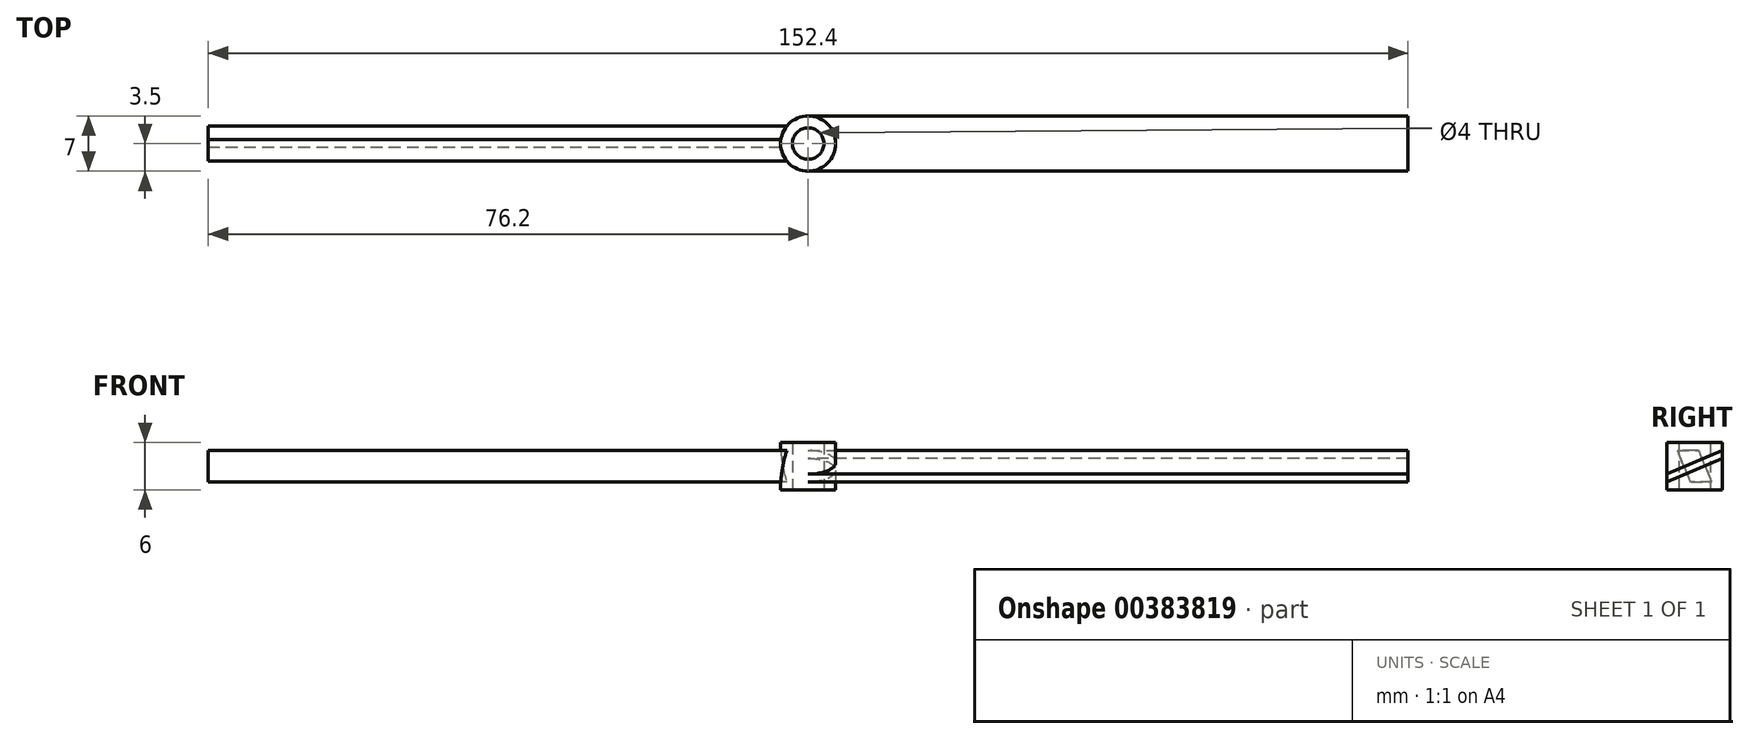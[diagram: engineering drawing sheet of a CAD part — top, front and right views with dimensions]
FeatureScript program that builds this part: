
annotation { "Feature Type Name" : "Feature", "Feature Type Description" : "" }
export const myFeature = defineFeature(function(context is Context, id is Id, definition is map)
    precondition{}
    {
        {
            var Q0;
            Q0=qCreatedBy(makeId("Top.planeOp"),FACE);
            var sketch = newSketch(context, id + "F0", { "sketchPlane" : qUnion([Q0])});
            skCircle(sketch, "E0", {"center": v(0, 0) * mm, "radius": 2 * mm});
            skLineSegment(sketch, "E1", {"start": v(0, 0) * mm, "end": v(2, 0) * mm});
            skLineSegment(sketch, "E2", {"start": v(0, 0) * mm, "end": v(76.2, 0) * mm});
            skLineSegment(sketch, "E3", {"start": v(0, 0) * mm, "end": v(-76.2, 0) * mm});
            skCircle(sketch, "E4", {"center": v(0, 0) * mm, "radius": 3.5 * mm});
            skLineSegment(sketch, "E5", {"start": v(0, 0) * mm, "end": v(0, 3.5) * mm});
            skLineSegment(sketch, "E6", {"start": v(0, 3.5) * mm, "end": v(0, -3.5) * mm});
            skLineSegment(sketch, "E7", {"start": v(0, 3.5) * mm, "end": v(-76.2, 3.5) * mm});
            skLineSegment(sketch, "E8", {"start": v(0, -3.5) * mm, "end": v(-76.2, -3.5) * mm});
            skLineSegment(sketch, "E9", {"start": v(-76.2, -3.5) * mm, "end": v(-76.2, 3.5) * mm});
            skLineSegment(sketch, "E10", {"start": v(0, 3.5) * mm, "end": v(76.2, 3.5) * mm});
            skLineSegment(sketch, "E11", {"start": v(0, -3.5) * mm, "end": v(76.2, -3.5) * mm});
            skLineSegment(sketch, "E12", {"start": v(76.2, -3.5) * mm, "end": v(76.2, 3.5) * mm});
            skSolve(sketch);
        }
        {
            var Q0;
            Q0=qSketchRegion(id+"F0",true);
            extrude(context, id + "F1", {"entities" : qUnion([Q0]), "depth" : 4 * mm});
        }
        {
            var Q0;
            Q0=makeQuery(id+"F1.opExtrude","CAP_FACE",FACE,{"disambiguationData":[OSD([sQuery(id+"F0.wireOp",EDGE,"E0"),sQuery(id+"F0.wireOp",EDGE,"E7"),sQuery(id+"F0.wireOp",EDGE,"E8"),sQuery(id+"F0.wireOp",EDGE,"E9"),sQuery(id+"F0.wireOp",EDGE,"E10"),sQuery(id+"F0.wireOp",EDGE,"E11"),sQuery(id+"F0.wireOp",EDGE,"E12")])],"isStart":false});
            var sketch = newSketch(context, id + "F2", { "sketchPlane" : qUnion([Q0])});
            skCircle(sketch, "E13", {"center": v(0, 0) * mm, "radius": 3.5 * mm});
            skLineSegment(sketch, "E14", {"start": v(0, 0) * mm, "end": v(3.5, 0) * mm});
            skLineSegment(sketch, "E15", {"start": v(3.5, 0) * mm, "end": v(-3.5, 0) * mm});
            skLineSegment(sketch, "E16", {"start": v(-3.5, 0) * mm, "end": v(-3.5, 3.5) * mm});
            skLineSegment(sketch, "E17", {"start": v(-3.5, 3.5) * mm, "end": v(-3.5, -3.5) * mm});
            skLineSegment(sketch, "E18", {"start": v(3.5, 0) * mm, "end": v(3.5, 3.5) * mm});
            skLineSegment(sketch, "E19", {"start": v(3.5, 3.5) * mm, "end": v(3.5, -3.5) * mm});
            skSolve(sketch);
        }
        {
            var Q0;
            {var subQ0=sQuery(id+"F2.wireOp",EDGE,"E17");var subQ1=sQuery(id+"F2.wireOp",EDGE,"E13");var subQ2=makeQuery(id+"F2.imprint","INTERSECT",VERTEX,{"derivedFrom":[subQ1,sQuery(id+"F2.wireOp",EDGE,"E15"),subQ0]});Q0=makeQuery(id+"F2.imprint","IMPRINT",FACE,{"disambiguationData":[TD([[makeQuery(id+"F2.imprint","IMPRINT",EDGE,{"disambiguationData":[TD([[subQ2,1.0]])],"derivedFrom":subQ1}),-1.0]])]});}
            var Q1;
            {var subQ0=sQuery(id+"F2.wireOp",EDGE,"E19");var subQ1=sQuery(id+"F2.wireOp",EDGE,"E13");var subQ2=makeQuery(id+"F2.imprint","INTERSECT",VERTEX,{"derivedFrom":[subQ1,sQuery(id+"F2.wireOp",EDGE,"E15"),subQ0]});Q1=makeQuery(id+"F2.imprint","IMPRINT",FACE,{"disambiguationData":[TD([[makeQuery(id+"F2.imprint","IMPRINT",EDGE,{"disambiguationData":[TD([[subQ2,-1.0]])],"derivedFrom":subQ1}),-1.0]])]});}
            var Q2;
            {var subQ0=sQuery(id+"F2.wireOp",EDGE,"E19");var subQ1=sQuery(id+"F2.wireOp",EDGE,"E13");var subQ2=makeQuery(id+"F2.imprint","INTERSECT",VERTEX,{"derivedFrom":[subQ1,sQuery(id+"F2.wireOp",EDGE,"E15"),subQ0]});Q2=makeQuery(id+"F2.imprint","IMPRINT",FACE,{"disambiguationData":[TD([[makeQuery(id+"F2.imprint","IMPRINT",EDGE,{"disambiguationData":[TD([[subQ2,1.0]])],"derivedFrom":subQ1}),-1.0]])]});}
            var Q3;
            {var subQ0=sQuery(id+"F2.wireOp",EDGE,"E17");var subQ1=sQuery(id+"F2.wireOp",EDGE,"E13");var subQ2=makeQuery(id+"F2.imprint","INTERSECT",VERTEX,{"derivedFrom":[subQ1,sQuery(id+"F2.wireOp",EDGE,"E15"),subQ0]});Q3=makeQuery(id+"F2.imprint","IMPRINT",FACE,{"disambiguationData":[TD([[makeQuery(id+"F2.imprint","IMPRINT",EDGE,{"disambiguationData":[TD([[subQ2,-1.0]])],"derivedFrom":subQ1}),-1.0]])]});}
            var Q4;
            {var subQ0=sQuery(id+"F2.wireOp",EDGE,"E15");var subQ3=makeQuery(id+"F1.opExtrude","CAP_EDGE",EDGE,{"disambiguationData":[OSD([sQuery(id+"F0.wireOp",EDGE,"E0")])],"isStart":false});var subQ6=makeQuery(id+"F2.imprint","INTERSECT",VERTEX,{"disambiguationData":[OD(0.0)],"derivedFrom":[subQ3,subQ0]});Q4=makeQuery(id+"F2.imprint","IMPRINT",FACE,{"disambiguationData":[TD([[makeQuery(id+"F2.imprint","IMPRINT",EDGE,{"disambiguationData":[TD([[subQ6,-1.0]])],"derivedFrom":subQ3}),-1.0]])]});}
            var Q5;
            {var subQ0=sQuery(id+"F2.wireOp",EDGE,"E15");var subQ3=makeQuery(id+"F1.opExtrude","CAP_EDGE",EDGE,{"disambiguationData":[OSD([sQuery(id+"F0.wireOp",EDGE,"E0")])],"isStart":false});var subQ5=makeQuery(id+"F2.imprint","INTERSECT",VERTEX,{"disambiguationData":[OD(0.0)],"derivedFrom":[subQ3,subQ0]});Q5=makeQuery(id+"F2.imprint","IMPRINT",FACE,{"disambiguationData":[TD([[makeQuery(id+"F2.imprint","IMPRINT",EDGE,{"disambiguationData":[TD([[subQ5,1.0]])],"derivedFrom":subQ3}),-1.0]])]});}
            extrude(context, id + "F3", {"entities" : qUnion([Q0, Q1, Q2, Q3, Q4, Q5]), "operationType" : NewBodyOperationType.ADD, "depth" : 1 * mm});
        }
        {
            var Q0;
            {var subQ0=sQuery(id+"F0.wireOp",EDGE,"E12");var subQ1=sQuery(id+"F0.wireOp",EDGE,"E11");var subQ2=sQuery(id+"F0.wireOp",EDGE,"E8");Q0=makeQuery(id+"F3.boolean.opBoolean","SPLIT",EDGE,{"disambiguationData":[TD([makeQuery(id+"F1.opExtrude","SWEPT_FACE",FACE,{"disambiguationData":[OSD([subQ0])]})])],"derivedFrom":makeQuery(id+"F1.opExtrude","CAP_EDGE",EDGE,{"disambiguationData":[OSD([subQ2,subQ1])],"isStart":false})});}
            chamfer(context, id + "F4", {"entities" : qUnion([Q0]), "chamferType" : ChamferType.TWO_OFFSETS, "width1" : 7 * mm, "oppositeDirection" : false, "width2" : 3 * mm, "tangentPropagation" : true});
        }
        {
            var Q0;
            {var subQ0=sQuery(id+"F0.wireOp",EDGE,"E9");var subQ1=sQuery(id+"F0.wireOp",EDGE,"E10");var subQ2=sQuery(id+"F0.wireOp",EDGE,"E7");Q0=makeQuery(id+"F3.boolean.opBoolean","SPLIT",EDGE,{"disambiguationData":[TD([makeQuery(id+"F1.opExtrude","SWEPT_FACE",FACE,{"disambiguationData":[OSD([subQ0])]})])],"derivedFrom":makeQuery(id+"F1.opExtrude","CAP_EDGE",EDGE,{"disambiguationData":[OSD([subQ2,subQ1])],"isStart":false})});}
            chamfer(context, id + "F5", {"entities" : qUnion([Q0]), "chamferType" : ChamferType.TWO_OFFSETS, "width1" : 3 * mm, "oppositeDirection" : false, "width2" : 7 * mm, "tangentPropagation" : true});
        }
        {
            var Q0;
            Q0=makeQuery(id+"F1.opExtrude","CAP_FACE",FACE,{"disambiguationData":[OSD([sQuery(id+"F0.wireOp",EDGE,"E0"),sQuery(id+"F0.wireOp",EDGE,"E7"),sQuery(id+"F0.wireOp",EDGE,"E8"),sQuery(id+"F0.wireOp",EDGE,"E9"),sQuery(id+"F0.wireOp",EDGE,"E10"),sQuery(id+"F0.wireOp",EDGE,"E11"),sQuery(id+"F0.wireOp",EDGE,"E12")])],"isStart":true});
            var sketch = newSketch(context, id + "F6", { "sketchPlane" : qUnion([Q0])});
            skCircle(sketch, "E20.cCircle", {"center": v(0, 0) * mm, "radius": 3.5 * mm, "construction": true});
            skLineSegment(sketch, "E20.0", {"start": v(3.5, -3.5) * mm, "end": v(-3.5, -3.5) * mm});
            skLineSegment(sketch, "E20.1", {"start": v(-3.5, -3.5) * mm, "end": v(-3.5, 3.5) * mm});
            skLineSegment(sketch, "E20.2", {"start": v(-3.5, 3.5) * mm, "end": v(3.5, 3.5) * mm});
            skLineSegment(sketch, "E20.3", {"start": v(3.5, 3.5) * mm, "end": v(3.5, -3.5) * mm});
            skPoint(sketch, "E20.0.midPoint", {"position": v(0, -3.5) * mm});
            skSolve(sketch);
        }
        {
            var Q0;
            Q0=makeQuery(id+"F6.imprint","IMPRINT",FACE,{"disambiguationData":[TD([[makeQuery(id+"F6.imprint","IMPRINT",EDGE,{"derivedFrom":sQuery(id+"F6.wireOp",EDGE,"E20.0")}),1.0]])]});
            extrude(context, id + "F7", {"entities" : qUnion([Q0]), "operationType" : NewBodyOperationType.ADD, "depth" : 1 * mm});
        }
        {
            var Q0;
            {var subQ0=sQuery(id+"F0.wireOp",EDGE,"E10");var subQ1=sQuery(id+"F0.wireOp",EDGE,"E7");var subQ2=sQuery(id+"F0.wireOp",EDGE,"E12");Q0=makeQuery(id+"F7.boolean.opBoolean","SPLIT",EDGE,{"disambiguationData":[TD([makeQuery(id+"F1.opExtrude","SWEPT_FACE",FACE,{"disambiguationData":[OSD([subQ2])]})])],"derivedFrom":makeQuery(id+"F1.opExtrude","CAP_EDGE",EDGE,{"disambiguationData":[OSD([subQ1,subQ0])],"isStart":true})});}
            chamfer(context, id + "F8", {"entities" : qUnion([Q0]), "chamferType" : ChamferType.TWO_OFFSETS, "width1" : 7 * mm, "oppositeDirection" : false, "width2" : 3 * mm, "tangentPropagation" : true});
        }
        {
            var Q0;
            {var subQ0=sQuery(id+"F0.wireOp",EDGE,"E11");var subQ1=sQuery(id+"F0.wireOp",EDGE,"E8");var subQ2=sQuery(id+"F0.wireOp",EDGE,"E9");Q0=makeQuery(id+"F7.boolean.opBoolean","SPLIT",EDGE,{"disambiguationData":[TD([makeQuery(id+"F1.opExtrude","SWEPT_FACE",FACE,{"disambiguationData":[OSD([subQ2])]})])],"derivedFrom":makeQuery(id+"F1.opExtrude","CAP_EDGE",EDGE,{"disambiguationData":[OSD([subQ1,subQ0])],"isStart":true})});}
            chamfer(context, id + "F9", {"entities" : qUnion([Q0]), "chamferType" : ChamferType.TWO_OFFSETS, "width1" : 3 * mm, "oppositeDirection" : false, "width2" : 7 * mm, "tangentPropagation" : true});
        }
        {
            var Q0;
            Q0=makeQuery(id+"F7.opExtrude","SWEPT_EDGE",EDGE,{"disambiguationData":[OSD([sQuery(id+"F0.wireOp",EDGE,"E8"),sQuery(id+"F0.wireOp",EDGE,"E11"),sQuery(id+"F6.wireOp",EDGE,"E20.2"),sQuery(id+"F6.wireOp",EDGE,"E20.3")])]});
            var Q1;
            Q1=makeQuery(id+"F7.opExtrude","SWEPT_EDGE",EDGE,{"disambiguationData":[OSD([sQuery(id+"F0.wireOp",EDGE,"E8"),sQuery(id+"F0.wireOp",EDGE,"E11"),sQuery(id+"F6.wireOp",EDGE,"E20.1"),sQuery(id+"F6.wireOp",EDGE,"E20.2")])]});
            var Q2;
            Q2=makeQuery(id+"F3.opExtrude","SWEPT_EDGE",EDGE,{"disambiguationData":[OSD([sQuery(id+"F0.wireOp",EDGE,"E8"),sQuery(id+"F0.wireOp",EDGE,"E11"),sQuery(id+"F2.wireOp",EDGE,"E17")])]});
            var Q3;
            Q3=makeQuery(id+"F3.opExtrude","SWEPT_EDGE",EDGE,{"disambiguationData":[OSD([sQuery(id+"F0.wireOp",EDGE,"E8"),sQuery(id+"F0.wireOp",EDGE,"E11"),sQuery(id+"F2.wireOp",EDGE,"E19")])]});
            var Q4;
            Q4=makeQuery(id+"F7.opExtrude","SWEPT_EDGE",EDGE,{"disambiguationData":[OSD([sQuery(id+"F0.wireOp",EDGE,"E7"),sQuery(id+"F0.wireOp",EDGE,"E10"),sQuery(id+"F6.wireOp",EDGE,"E20.0"),sQuery(id+"F6.wireOp",EDGE,"E20.3")])]});
            var Q5;
            Q5=makeQuery(id+"F3.opExtrude","SWEPT_EDGE",EDGE,{"disambiguationData":[OSD([sQuery(id+"F0.wireOp",EDGE,"E7"),sQuery(id+"F0.wireOp",EDGE,"E10"),sQuery(id+"F2.wireOp",EDGE,"E19")])]});
            var Q6;
            Q6=makeQuery(id+"F3.opExtrude","SWEPT_EDGE",EDGE,{"disambiguationData":[OSD([sQuery(id+"F0.wireOp",EDGE,"E7"),sQuery(id+"F0.wireOp",EDGE,"E10"),sQuery(id+"F2.wireOp",EDGE,"E17")])]});
            var Q7;
            Q7=makeQuery(id+"F7.opExtrude","SWEPT_EDGE",EDGE,{"disambiguationData":[OSD([sQuery(id+"F0.wireOp",EDGE,"E7"),sQuery(id+"F0.wireOp",EDGE,"E10"),sQuery(id+"F6.wireOp",EDGE,"E20.0"),sQuery(id+"F6.wireOp",EDGE,"E20.1")])]});
            fillet(context, id + "F10", {"entities" : qUnion([Q0, Q1, Q2, Q3, Q4, Q5, Q6, Q7]), "radius" : 3.5 * mm, "tangentPropagation" : true, "allowEdgeOverflow" : false});
        }
    });
